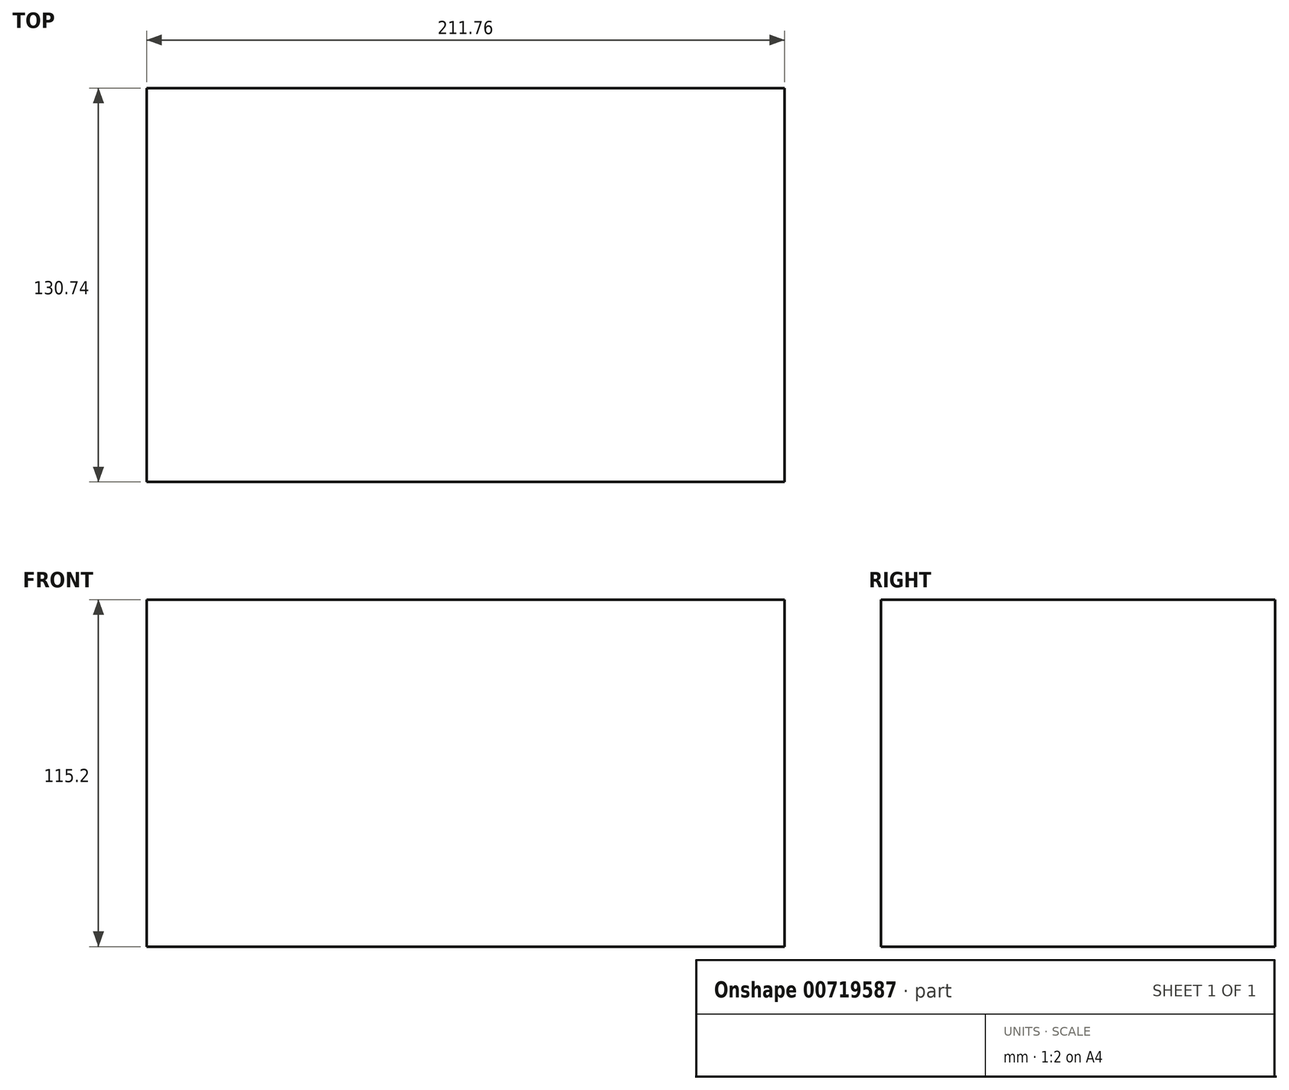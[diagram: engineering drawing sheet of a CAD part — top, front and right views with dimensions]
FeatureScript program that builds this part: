
annotation { "Feature Type Name" : "Feature", "Feature Type Description" : "" }
export const myFeature = defineFeature(function(context is Context, id is Id, definition is map)
    precondition{}
    {
        {
            var Q0;
            Q0=qCreatedBy(makeId("Top.planeOp"),FACE);
            var sketch = newSketch(context, id + "F0", { "sketchPlane" : qUnion([Q0])});
            skLineSegment(sketch, "E0.bottom", {"start": v(-105.88, 65.37) * mm, "end": v(105.88, 65.37) * mm});
            skLineSegment(sketch, "E0.top", {"start": v(-105.88, -65.37) * mm, "end": v(105.88, -65.37) * mm});
            skLineSegment(sketch, "E0.left", {"start": v(-105.88, 65.37) * mm, "end": v(-105.88, -65.37) * mm});
            skLineSegment(sketch, "E0.right", {"start": v(105.88, 65.37) * mm, "end": v(105.88, -65.37) * mm});
            skPoint(sketch, "E0.middle", {"position": v(0, 0) * mm});
            skSolve(sketch);
        }
        {
            var Q0;
            Q0 = qSketchRegion(id + "F0", true);
            extrude(context, id + "F1", {"entities" : qUnion([Q0]), "depth" : 115.2 * mm, "offsetDistance" : 25 * mm});
        }
    });
